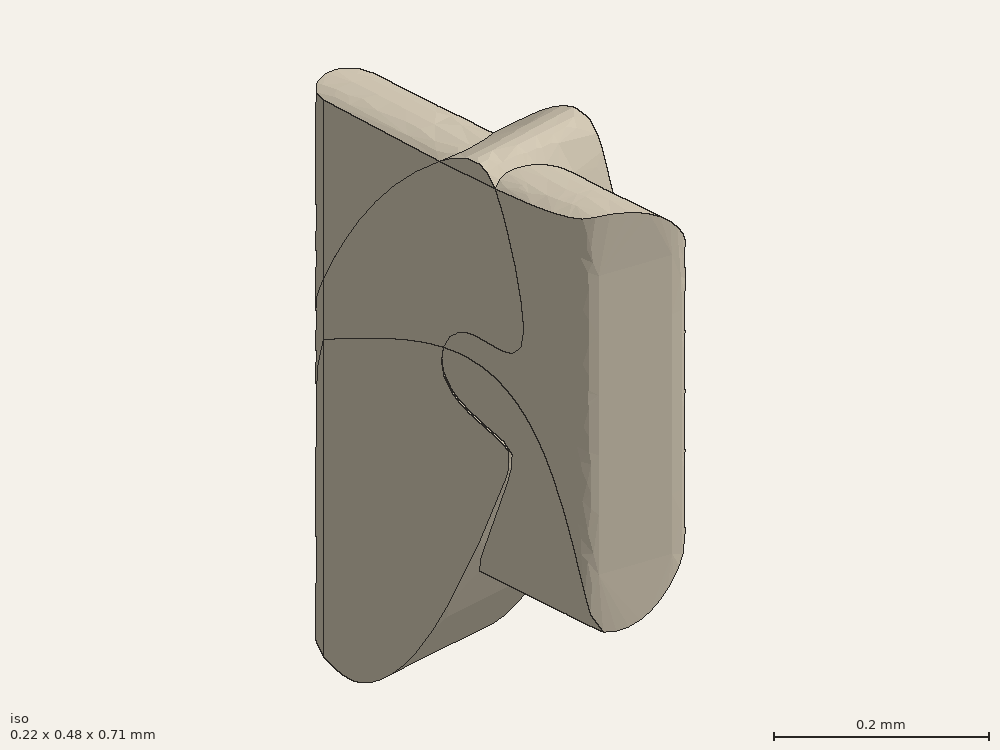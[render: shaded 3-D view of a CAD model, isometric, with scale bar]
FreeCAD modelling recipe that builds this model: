
FCSTD DOCUMENT  (FreeCAD 2021.0202R23662 +3181 (Git))
Label: tinytrax_02
License: All rights reserved
LicenseURL: http://en.wikipedia.org/wiki/All_rights_reserved
objects: PartDesign::Body×4, Sketcher::SketchObject×3, PartDesign::Pad×3, Mesh::Feature×1, Part::MultiCommon×1
note: 17 computed .brp shape members not serialized (recipe doc carries the construction recipe); baked Part::Feature solids carry a one-line shape summary decoded from their .brp

FEATURE [Mesh::Feature] model
FEATURE [PartDesign::Body] Body
  AutoGroupSolids = false
  ExportMode = 0
  Origin = -> Origin
  _GroupVersion = 1
FEATURE [Sketcher::SketchObject] Sketch
  FullyConstrained = false
  MapMode = 5
  Support = -> [XY_Plane001]
  sketch-geometry (20):
    g0-g9: Circle [constr] x10 (B-spline internal-alignment scaffolding for g10; pole/knot coordinates omitted)
    g10: BSplineCurve PolesCount=10 KnotsCount=8 Degree=3 IsPeriodic=0
    g11-g18: GeomPoint [constr] x8 (B-spline internal-alignment scaffolding for g10; pole/knot coordinates omitted)
    g19: LineSegment [constr] StartX=0.16 StartY=0.054445 StartZ=0 EndX=0.16 EndY=-0.65274 EndZ=0
  constraints (8):
    c: Weight(g0) = 1
    c: Equal(g0, g1-g9) x9
    c: Coincident(g9,g0)
    c: InternalAlignment(g0-g9 -> g10) x10
    c: InternalAlignment(g11-g18 -> g10) x8
    c: Vertical(g10,g8)
    c: Vertical(g19)
    c: DistanceX(g-1,g19) = 0.16
FEATURE [Sketcher::SketchObject] Sketch001
  FullyConstrained = false
  MapMode = 5
  Placement = pos=(0,0,0) rot=(0.57735,0.57735,0.57735;2.0944rad)
  Support = -> [YZ_Plane003]
  sketch-geometry (27):
    g0-g13: Circle [constr] x14 (B-spline internal-alignment scaffolding for g14; pole/knot coordinates omitted)
    g14: BSplineCurve PolesCount=14 KnotsCount=12 Degree=3 IsPeriodic=0
    g15-g26: GeomPoint [constr] x12 (B-spline internal-alignment scaffolding for g14; pole/knot coordinates omitted)
  constraints (5):
    c: Weight(g0) = 1
    c: Equal(g0, g1-g13) x13
    c: Coincident(g13,g0)
    c: InternalAlignment(g0-g13 -> g14) x14
    c: InternalAlignment(g15-g26 -> g14) x12
FEATURE [Sketcher::SketchObject] Sketch002
  FullyConstrained = false
  MapMode = 5
  Placement = pos=(0,0,0) rot=(1,0,0;1.5708rad)
  Support = -> [XZ_Plane002]
  sketch-geometry (17):
    g0-g8: Circle [constr] x9 (B-spline internal-alignment scaffolding for g9; pole/knot coordinates omitted)
    g9: BSplineCurve PolesCount=9 KnotsCount=7 Degree=3 IsPeriodic=0
    g10-g16: GeomPoint [constr] x7 (B-spline internal-alignment scaffolding for g9; pole/knot coordinates omitted)
  constraints (6):
    c: Weight(g0) = 1
    c: Equal(g0, g1-g8) x8
    c: InternalAlignment(g0-g8 -> g9) x9
    c: InternalAlignment(g10-g16 -> g9) x7
    c: Coincident(g9,g9)
    c: Vertical(g1,g9)
FEATURE [PartDesign::Pad] Pad
  ClaimChildren = false
  Direction = (1,1,1)
  Fit = 0
  FitJoin = 0
  InnerFit = 0
  InnerFitJoin = 0
  InnerTaperAngle = 0
  InnerTaperAngleRev = 0
  Length = 1
  Length2 = 100
  Midplane = true
  NewSolid = false
  Profile = -> Sketch
  Suppress = false
  Type = 0
FEATURE [PartDesign::Body] Body001  label="BodyFront"
  AutoGroupSolids = false
  ExportMode = 0
  Group = -> [Sketch,Pad]
  Origin = -> Origin001
  Tip = -> Pad
  _ExportChildren = -> [Pad]
  _GroupVersion = 1
FEATURE [PartDesign::Pad] Pad001
  ClaimChildren = false
  Direction = (1,1,1)
  Fit = 0
  FitJoin = 0
  InnerFit = 0
  InnerFitJoin = 0
  InnerTaperAngle = 0
  InnerTaperAngleRev = 0
  Length = 1
  Length2 = 100
  Midplane = true
  NewSolid = false
  Placement = pos=(0,0,0) rot=(1,0,0;1.5708rad)
  Profile = -> Sketch002
  Suppress = false
  Type = 0
FEATURE [PartDesign::Body] Body002  label="BodyTop"
  AutoGroupSolids = false
  ExportMode = 0
  Group = -> [Sketch002,Pad001]
  Origin = -> Origin002
  Tip = -> Pad001
  _ExportChildren = -> [Pad001]
  _GroupVersion = 1
FEATURE [PartDesign::Pad] Pad002
  ClaimChildren = false
  Direction = (1,1,1)
  Fit = 0
  FitJoin = 0
  InnerFit = 0
  InnerFitJoin = 0
  InnerTaperAngle = 0
  InnerTaperAngleRev = 0
  Length = 1
  Length2 = 100
  Midplane = true
  NewSolid = false
  Placement = pos=(0,0,0) rot=(0.57735,0.57735,0.57735;2.0944rad)
  Profile = -> Sketch001
  Suppress = false
  Type = 0
FEATURE [PartDesign::Body] Body003  label="BodySide"
  AutoGroupSolids = false
  ExportMode = 0
  Group = -> [Sketch001,Pad002]
  Origin = -> Origin003
  Tip = -> Pad002
  _ExportChildren = -> [Pad002]
  _GroupVersion = 1
FEATURE [Part::MultiCommon] Common
  Shapes = -> [Body001,Body002,Body003]
